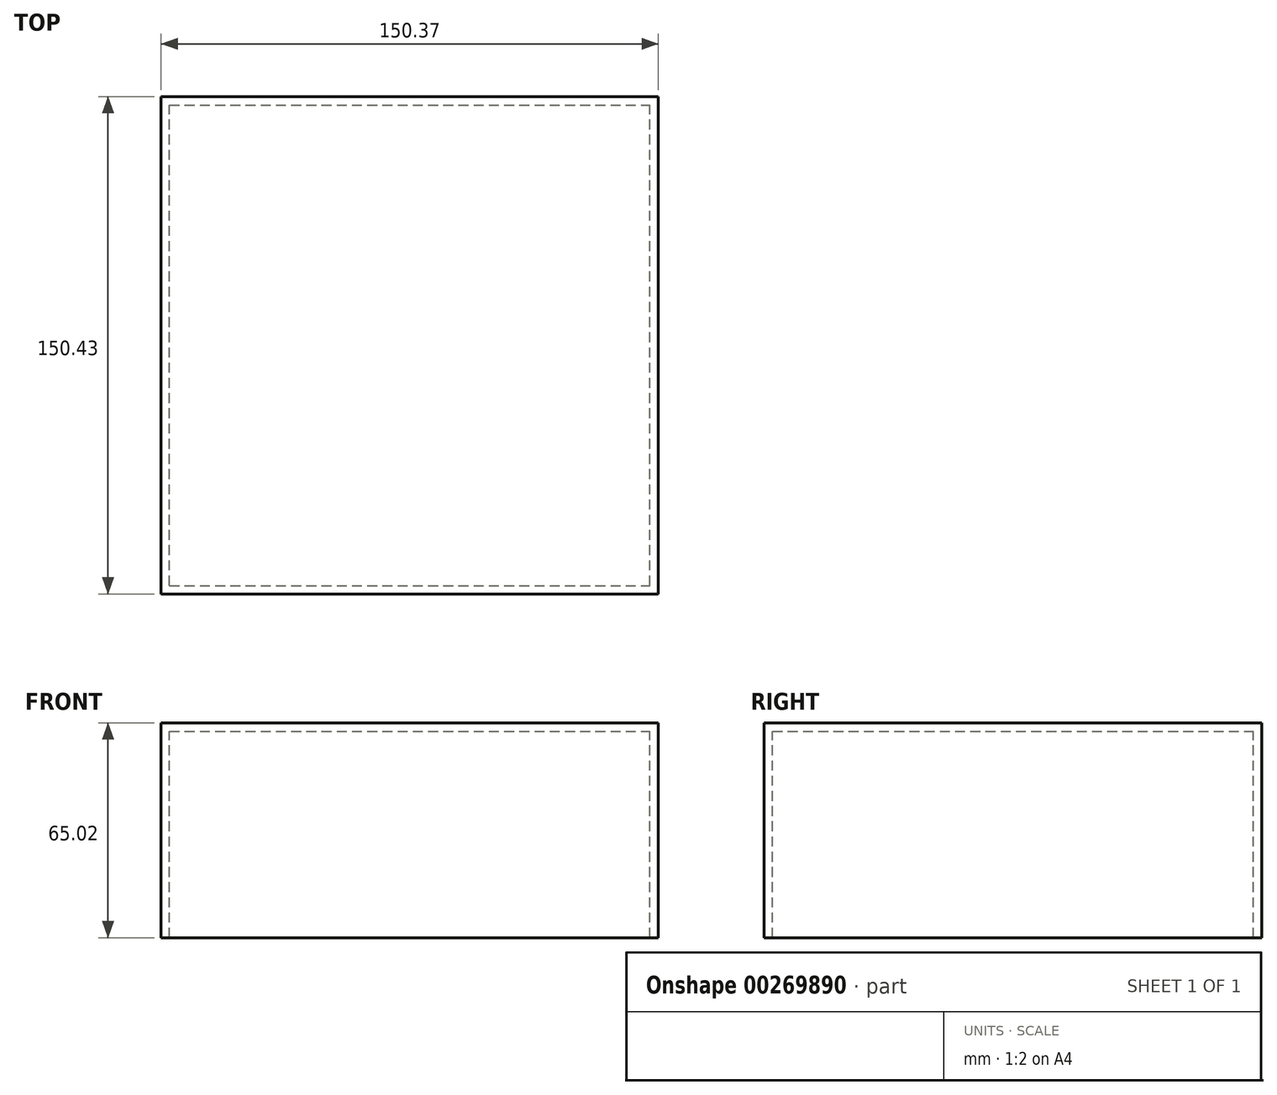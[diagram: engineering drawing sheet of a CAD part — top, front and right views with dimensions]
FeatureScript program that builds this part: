
annotation { "Feature Type Name" : "Feature", "Feature Type Description" : "" }
export const myFeature = defineFeature(function(context is Context, id is Id, definition is map)
    precondition{}
    {
        {
            var Q0;
            Q0=qCreatedBy(makeId("Top.planeOp"),FACE);
            var sketch = newSketch(context, id + "F0", { "sketchPlane" : qUnion([Q0])});
            skLineSegment(sketch, "E0.bottom", {"start": v(-74.2, -74.65) * mm, "end": v(76.16, -74.65) * mm});
            skLineSegment(sketch, "E0.top", {"start": v(-74.2, 75.78) * mm, "end": v(76.16, 75.78) * mm});
            skLineSegment(sketch, "E0.left", {"start": v(-74.2, -74.65) * mm, "end": v(-74.2, 75.78) * mm});
            skLineSegment(sketch, "E0.right", {"start": v(76.16, -74.65) * mm, "end": v(76.16, 75.78) * mm});
            skSolve(sketch);
        }
        {
            var Q0;
            Q0=makeQuery(id+"F0.imprint","IMPRINT",FACE,{"disambiguationData":[TD([[makeQuery(id+"F0.imprint","IMPRINT",EDGE,{"derivedFrom":sQuery(id+"F0.wireOp",EDGE,"E0.bottom")}),1.0]])]});
            extrude(context, id + "F1", {"entities" : qUnion([Q0]), "oppositeDirection" : true, "depth" : 65.02 * mm});
        }
        {
            var Q0;
            Q0=makeQuery(id+"F1.opExtrude","CAP_FACE",FACE,{"disambiguationData":[OSD([sQuery(id+"F0.wireOp",EDGE,"E0.bottom"),sQuery(id+"F0.wireOp",EDGE,"E0.top"),sQuery(id+"F0.wireOp",EDGE,"E0.left"),sQuery(id+"F0.wireOp",EDGE,"E0.right")])],"isStart":false});
            shell(context, id + "F2", {"entities" : qUnion([Q0]), "thickness" : 2.54 * mm});
        }
    });
